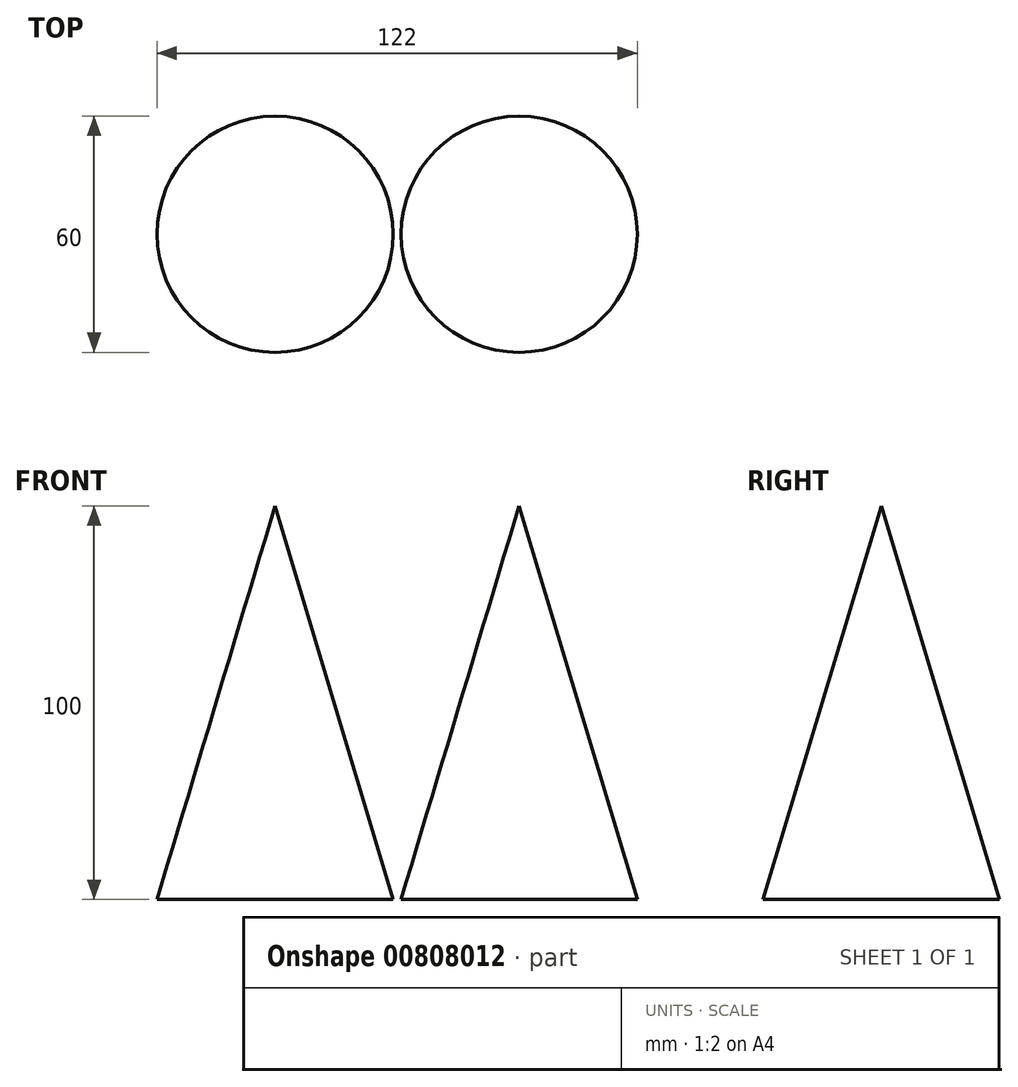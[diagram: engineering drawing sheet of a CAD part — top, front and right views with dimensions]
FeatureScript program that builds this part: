
annotation { "Feature Type Name" : "Feature", "Feature Type Description" : "" }
export const myFeature = defineFeature(function(context is Context, id is Id, definition is map)
    precondition{}
    {
        {
            var Q0;
            Q0=qCreatedBy(makeId("Top.planeOp"),FACE);
            var sketch = newSketch(context, id + "F0", { "sketchPlane" : qUnion([Q0])});
            skCircle(sketch, "E0", {"center": v(0, 0) * mm, "radius": 30 * mm});
            skLineSegment(sketch, "E1", {"start": v(0, 0) * mm, "end": v(-62, 0) * mm});
            skCircle(sketch, "E2", {"center": v(-62, 0) * mm, "radius": 30 * mm});
            skSolve(sketch);
        }
        {
            var Q0;
            Q0=qCreatedBy(makeId("Top.planeOp"),FACE);
            cPlane(context, id + "F1", {"entities" : qUnion([Q0]), "cplaneType" : CPlaneType.OFFSET, "offset" : 100 * mm, "width" : 150 * mm, "height" : 150 * mm});
        }
        {
            var Q0;
            Q0=qCreatedBy(id+"F1.planeOp",FACE);
            var sketch = newSketch(context, id + "F2", { "sketchPlane" : qUnion([Q0])});
            skPoint(sketch, "E3.0", {"position": v(0, 0) * mm});
            skPoint(sketch, "E4.0", {"position": v(-62, 0) * mm});
            skSolve(sketch);
        }
        {
            var Q0;
            Q0=makeQuery(id+"F0.imprint","IMPRINT",FACE,{"disambiguationData":[TD([[makeQuery(id+"F0.imprint","IMPRINT",EDGE,{"derivedFrom":sQuery(id+"F0.wireOp",EDGE,"E0")}),1.0]])]});
            var Q1;
            Q1=sQuery(id+"F2.wireOp",VERTEX,"E3.0");
            loft(context, id + "F3", {"sheetProfilesArray" : [{ "sheetProfileEntities" : qUnion([Q0]) }, { "sheetProfileEntities" : qUnion([Q1]) }]});
        }
        {
            var Q0;
            Q0=makeQuery(id+"F0.imprint","IMPRINT",FACE,{"disambiguationData":[TD([[makeQuery(id+"F0.imprint","IMPRINT",EDGE,{"derivedFrom":sQuery(id+"F0.wireOp",EDGE,"E2")}),1.0]])]});
            var Q1;
            Q1=sQuery(id+"F2.wireOp",VERTEX,"E4.0");
            loft(context, id + "F4", {"sheetProfilesArray" : [{ "sheetProfileEntities" : qUnion([Q0]) }, { "sheetProfileEntities" : qUnion([Q1]) }]});
        }
    });
